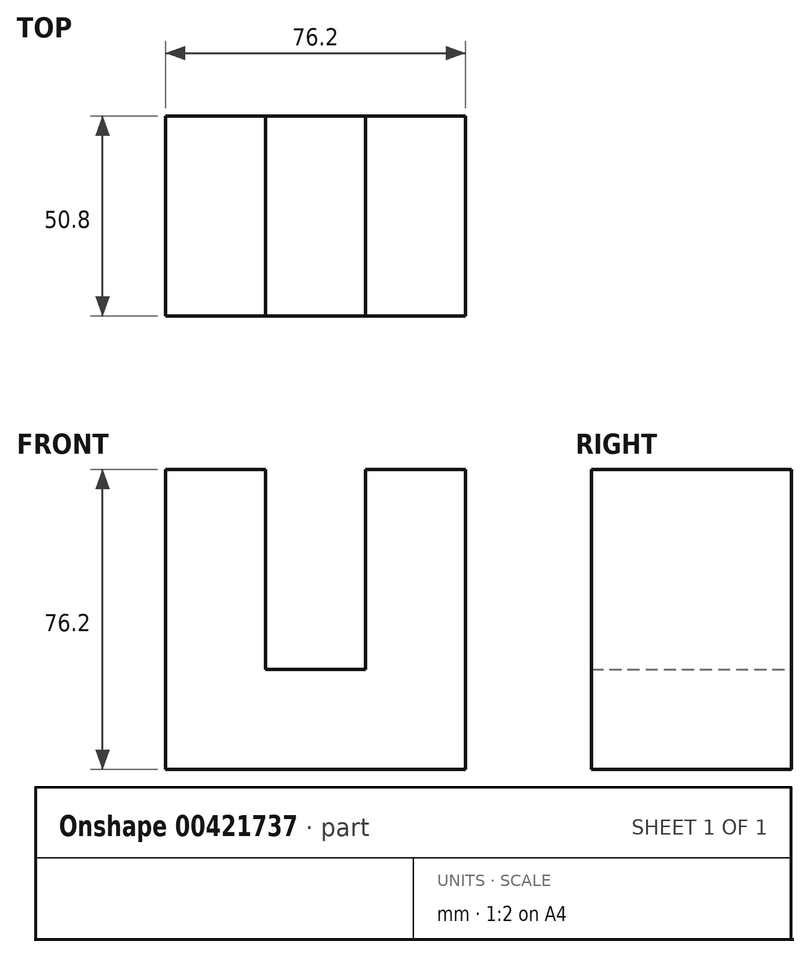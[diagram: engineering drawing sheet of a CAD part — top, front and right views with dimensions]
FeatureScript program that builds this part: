
annotation { "Feature Type Name" : "Feature", "Feature Type Description" : "" }
export const myFeature = defineFeature(function(context is Context, id is Id, definition is map)
    precondition{}
    {
        {
            var Q0;
            Q0=qCreatedBy(makeId("Front.planeOp"),FACE);
            var sketch = newSketch(context, id + "F0", { "sketchPlane" : qUnion([Q0])});
            skLineSegment(sketch, "E0", {"start": v(0, 0) * mm, "end": v(76.2, 0) * mm});
            skLineSegment(sketch, "E1", {"start": v(0, 0) * mm, "end": v(0, 76.2) * mm});
            skLineSegment(sketch, "E2", {"start": v(0, 76.2) * mm, "end": v(25.4, 76.2) * mm});
            skLineSegment(sketch, "E3", {"start": v(25.4, 76.2) * mm, "end": v(25.4, 25.4) * mm});
            skLineSegment(sketch, "E4", {"start": v(25.4, 25.4) * mm, "end": v(50.8, 25.4) * mm});
            skLineSegment(sketch, "E5", {"start": v(50.8, 25.4) * mm, "end": v(50.8, 76.2) * mm});
            skLineSegment(sketch, "E6", {"start": v(50.8, 76.2) * mm, "end": v(76.2, 76.2) * mm});
            skLineSegment(sketch, "E7", {"start": v(76.2, 76.2) * mm, "end": v(76.2, 0) * mm});
            skSolve(sketch);
        }
        {
            var Q0;
            Q0 = qSketchRegion(id + "F0", true);
            extrude(context, id + "F1", {"entities" : qUnion([Q0]), "depth" : 50.8 * mm});
        }
    });
